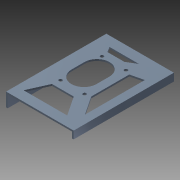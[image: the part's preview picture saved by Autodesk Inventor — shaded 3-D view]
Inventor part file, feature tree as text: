
AUTODESK INVENTOR PART (.ipt)
format: ipt  version: 2013 (Build 170138000, 138)  size: 162,816 bytes
history: native  units: mm
features: sketch x5, extrude x4, other x1, hole x1
ambient origin geometry x1: Origin
feature tree (11):
  other  "ソリッド1"
  extrude  "押し出し1"  Depth=92.0mm
  hole  "穴1"  [1 undecoded]
  extrude  "押し出し3"  Depth=62.0mm
  extrude  "押し出し5"  Depth=31.0mm
  extrude  "押し出し7"  Depth=1.5mm TaperAngle=0.0deg
  sketch  "スケッチ1"
  sketch  "スケッチ3"
  sketch  "スケッチ4"
  sketch  "スケッチ6"
  sketch  "スケッチ7"
note: 1 required parameter value undecoded (feature->parameter linkage not recoverable at this tier; creation-order binding heuristic only, values carry confidence <= 0.55)
